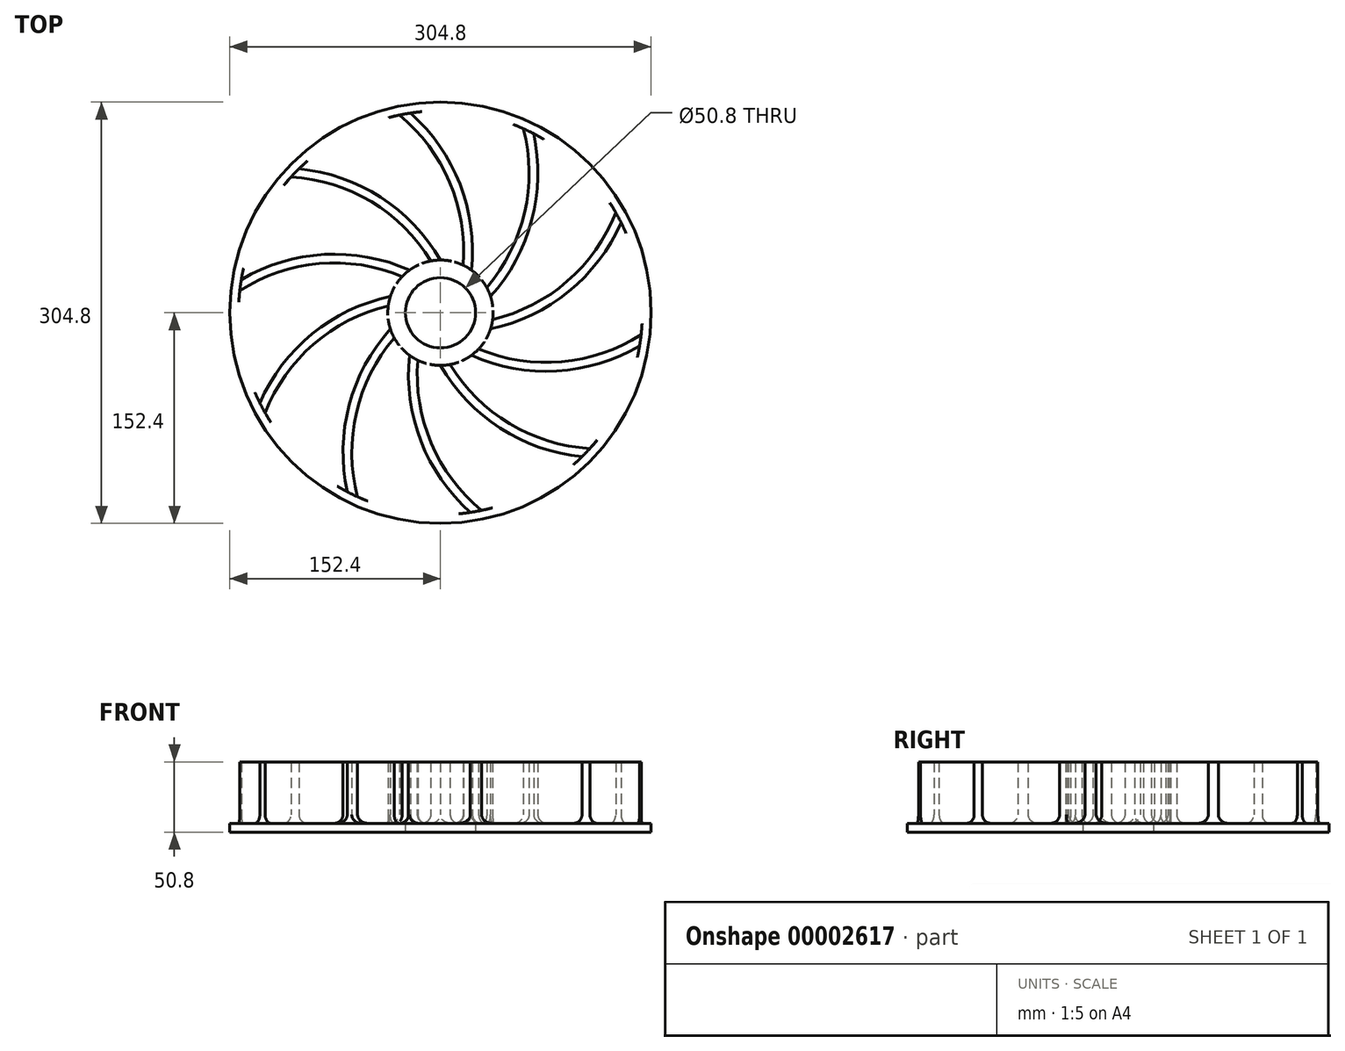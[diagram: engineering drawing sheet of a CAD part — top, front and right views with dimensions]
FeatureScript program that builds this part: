
annotation { "Feature Type Name" : "Feature", "Feature Type Description" : "" }
export const myFeature = defineFeature(function(context is Context, id is Id, definition is map)
    precondition{}
    {
        {
            var Q0;
            Q0=qCreatedBy(makeId("Top.planeOp"),FACE);
            var sketch = newSketch(context, id + "F0", { "sketchPlane" : qUnion([Q0])});
            skCircle(sketch, "E0.0", {"center": v(0, 0) * mm, "radius": 146.05 * mm});
            skCircle(sketch, "E1", {"center": v(0, 0) * mm, "radius": 25.4 * mm});
            skCircle(sketch, "E2", {"center": v(0, 0) * mm, "radius": 38.1 * mm});
            skLineSegment(sketch, "E3", {"start": v(0, 146.05) * mm, "end": v(0, -146.05) * mm, "construction": true});
            skLineSegment(sketch, "E4", {"start": v(-146.05, 0) * mm, "end": v(146.05, 0) * mm, "construction": true});
            skLineSegment(sketch, "E5", {"start": v(0, 38.1) * mm, "end": v(33, -19.05) * mm, "construction": true});
            skArc(sketch, "E6", {"start": v(0, 38.1) * mm, "mid": v(-43.22, 83.5) * mm, "end": v(-102.4, 104.13) * mm});
            skArc(sketch, "E7.0", {"start": v(-7, 37.45) * mm, "mid": v(-50.07, 80.28) * mm, "end": v(-108.1, 98.21) * mm});
            skCircle(sketch, "E8", {"center": v(0, 0) * mm, "radius": 152.4 * mm});
            skLineSegment(sketch, "E9", {"start": v(-7, 37.45) * mm, "end": v(-1.5, 40.63) * mm, "construction": true});
            skSolve(sketch);
        }
        {
            var Q0;
            {var subQ1=sQuery(id+"F0.wireOp",EDGE,"E6");Q0=makeQuery(id+"F0.imprint","IMPRINT",FACE,{"disambiguationData":[TD([[makeQuery(id+"F0.imprint","IMPRINT",EDGE,{"derivedFrom":subQ1}),-1.0]])]});}
            var Q1;
            Q1=makeQuery(id+"F0.imprint","IMPRINT",FACE,{"disambiguationData":[TD([[makeQuery(id+"F0.imprint","IMPRINT",EDGE,{"derivedFrom":sQuery(id+"F0.wireOp",EDGE,"E8")}),1.0]])]});
            var Q2;
            {var subQ1=sQuery(id+"F0.wireOp",EDGE,"E6");Q2=makeQuery(id+"F0.imprint","IMPRINT",FACE,{"disambiguationData":[TD([[makeQuery(id+"F0.imprint","IMPRINT",EDGE,{"derivedFrom":subQ1}),1.0]])]});}
            var Q3;
            Q3=makeQuery(id+"F0.imprint","IMPRINT",FACE,{"disambiguationData":[TD([[makeQuery(id+"F0.imprint","IMPRINT",EDGE,{"derivedFrom":sQuery(id+"F0.wireOp",EDGE,"E1")}),-1.0]])]});
            var Q4;
            {var subQ4=sQuery(id+"F0.wireOp",EDGE,"E7.0");Q4=makeQuery(id+"F0.imprint","IMPRINT",FACE,{"disambiguationData":[TD([[makeQuery(id+"F0.imprint","IMPRINT",EDGE,{"derivedFrom":subQ4}),-1.0]])]});}
            extrude(context, id + "F1", {"entities" : qUnion([Q0, Q1, Q2, Q3, Q4]), "depth" : 6.35 * mm});
        }
        {
            var Q0;
            {var subQ4=sQuery(id+"F0.wireOp",EDGE,"E7.0");Q0=makeQuery(id+"F0.imprint","IMPRINT",FACE,{"disambiguationData":[TD([[makeQuery(id+"F0.imprint","IMPRINT",EDGE,{"derivedFrom":subQ4}),-1.0]])]});}
            extrude(context, id + "F2", {"entities" : qUnion([Q0]), "operationType" : NewBodyOperationType.ADD, "depth" : 50.8 * mm});
        }
        {
            var Q0;
            Q0=makeQuery(id+"F2.boolean.opBoolean","INTERSECT",EDGE,{"derivedFrom":[makeQuery(id+"F1.opExtrude","CAP_FACE",FACE,{"disambiguationData":[OSD([sQuery(id+"F0.wireOp",EDGE,"E1"),sQuery(id+"F0.wireOp",EDGE,"E8")])],"isStart":false}),makeQuery(id+"F2.opExtrude","SWEPT_FACE",FACE,{"disambiguationData":[OSD([sQuery(id+"F0.wireOp",EDGE,"E7.0")])]})]});
            var Q1;
            Q1=makeQuery(id+"F2.boolean.opBoolean","INTERSECT",EDGE,{"derivedFrom":[makeQuery(id+"F1.opExtrude","CAP_FACE",FACE,{"disambiguationData":[OSD([sQuery(id+"F0.wireOp",EDGE,"E1"),sQuery(id+"F0.wireOp",EDGE,"E8")])],"isStart":false}),makeQuery(id+"F2.opExtrude","SWEPT_FACE",FACE,{"disambiguationData":[OSD([sQuery(id+"F0.wireOp",EDGE,"E6")])]})]});
            fillet(context, id + "F3", {"entities" : qUnion([Q0, Q1]), "radius" : 6.35 * mm, "tangentPropagation" : true, "allowEdgeOverflow" : false});
        }
        {
            var Q0;
            Q0=makeQuery(id+"F3.opFillet","BLEND_FACE",FACE,{"disambiguationData":[OSD([sQuery(id+"F0.wireOp",EDGE,"E1"),sQuery(id+"F0.wireOp",EDGE,"E7.0"),sQuery(id+"F0.wireOp",EDGE,"E8")])]});
            var Q1;
            Q1=makeQuery(id+"F2.opExtrude","SWEPT_FACE",FACE,{"disambiguationData":[OSD([sQuery(id+"F0.wireOp",EDGE,"E6")])]});
            var Q2;
            Q2=makeQuery(id+"F2.opExtrude","CAP_FACE",FACE,{"disambiguationData":[OSD([sQuery(id+"F0.wireOp",EDGE,"E0.0"),sQuery(id+"F0.wireOp",EDGE,"E2"),sQuery(id+"F0.wireOp",EDGE,"E6"),sQuery(id+"F0.wireOp",EDGE,"E7.0")])],"isStart":false});
            var Q3;
            Q3=makeQuery(id+"F2.opExtrude","SWEPT_FACE",FACE,{"disambiguationData":[OSD([sQuery(id+"F0.wireOp",EDGE,"E7.0")])]});
            var Q4;
            Q4=makeQuery(id+"F2.opExtrude","SWEPT_FACE",FACE,{"disambiguationData":[OSD([sQuery(id+"F0.wireOp",EDGE,"E0.0")])]});
            var Q5;
            Q5=makeQuery(id+"F3.opFillet","BLEND_FACE",FACE,{"disambiguationData":[OSD([sQuery(id+"F0.wireOp",EDGE,"E1"),sQuery(id+"F0.wireOp",EDGE,"E6"),sQuery(id+"F0.wireOp",EDGE,"E8")])]});
            var Q6;
            Q6=makeQuery(id+"F2.opExtrude","SWEPT_FACE",FACE,{"disambiguationData":[OSD([sQuery(id+"F0.wireOp",EDGE,"E2")])]});
            var Q7;
            Q7=makeQuery(id+"F1.opExtrude","CAP_EDGE",EDGE,{"disambiguationData":[OSD([sQuery(id+"F0.wireOp",EDGE,"E1")])],"isStart":true});
            circularPattern(context, id + "F4", {"faces" : qUnion([Q0, Q1, Q2, Q3, Q4, Q5, Q6]), "axis" : qUnion([Q7]), "angle" : 360 * degree, "instanceCount" : 10, "equalSpace" : true, "patternType" : PatternType.FACE});
        }
    });
